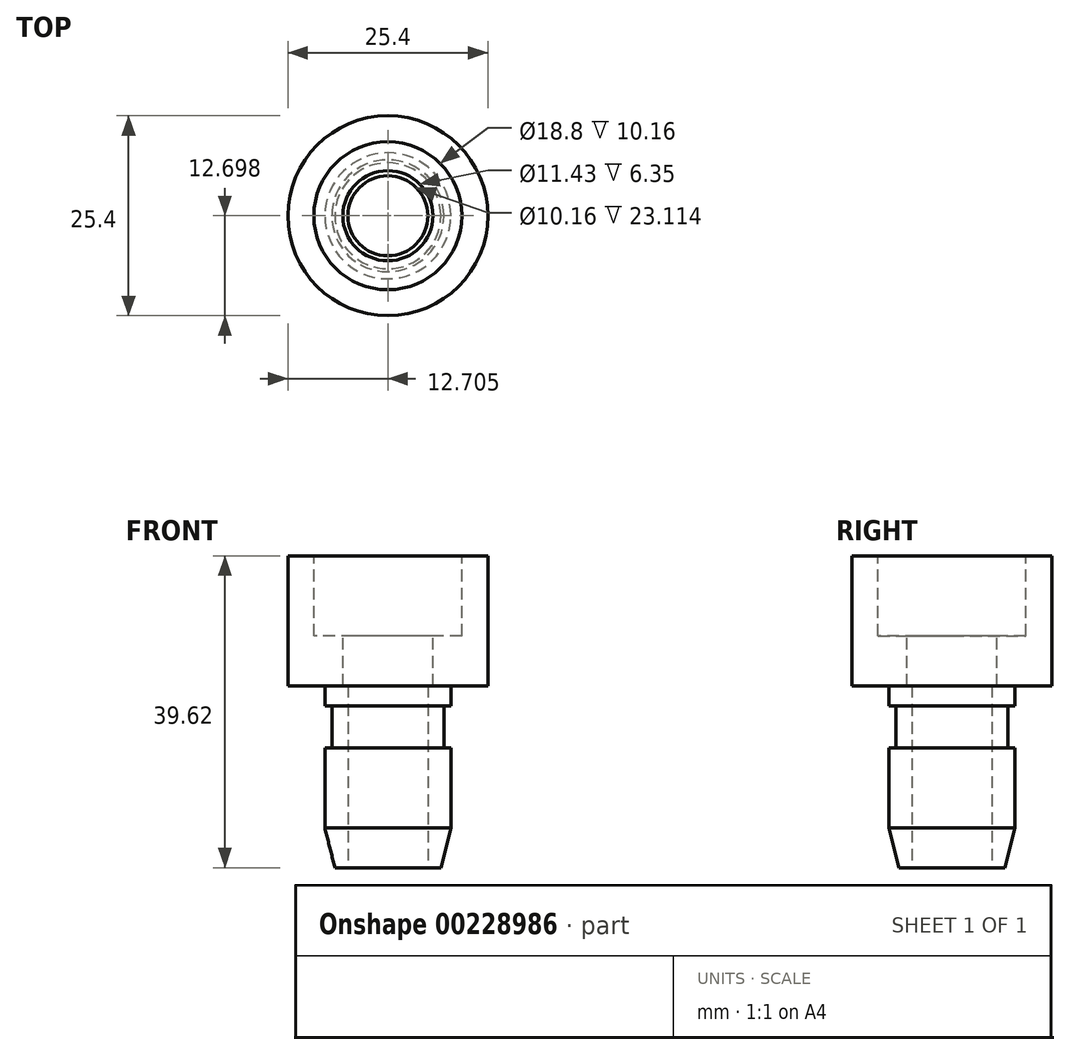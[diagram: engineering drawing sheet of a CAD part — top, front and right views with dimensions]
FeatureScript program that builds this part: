
annotation { "Feature Type Name" : "Feature", "Feature Type Description" : "" }
export const myFeature = defineFeature(function(context is Context, id is Id, definition is map)
    precondition{}
    {
        {
            var Q0;
            Q0=qCreatedBy(makeId("Top.planeOp"),FACE);
            var sketch = newSketch(context, id + "F0", { "sketchPlane" : qUnion([Q0])});
            skCircle(sketch, "E0", {"center": v(-47.56, -9.23) * mm, "radius": 12.7 * mm});
            skSolve(sketch);
        }
        {
            var Q0;
            Q0 = qSketchRegion(id + "F0", true);
            extrude(context, id + "F1", {"entities" : qUnion([Q0]), "oppositeDirection" : true, "depth" : 16.5 * mm});
        }
        {
            var Q0;
            Q0=makeQuery(id+"F1.opExtrude","CAP_FACE",FACE,{"disambiguationData":[OSD([sQuery(id+"F0.wireOp",EDGE,"E0")])],"isStart":true});
            var sketch = newSketch(context, id + "F2", { "sketchPlane" : qUnion([Q0])});
            skCircle(sketch, "E1", {"center": v(-47.56, -9.23) * mm, "radius": 9.4 * mm});
            skSolve(sketch);
        }
        {
            var Q0;
            Q0 = qSketchRegion(id + "F2", true);
            extrude(context, id + "F3", {"entities" : qUnion([Q0]), "operationType" : NewBodyOperationType.REMOVE, "oppositeDirection" : true, "depth" : 10.16 * mm});
        }
        {
            var Q0;
            Q0=makeQuery(id+"F3.boolean.opBoolean","COPY",FACE,{"derivedFrom":makeQuery(id+"F3.opExtrude","CAP_FACE",FACE,{"disambiguationData":[OSD([sQuery(id+"F2.wireOp",EDGE,"E1")])],"isStart":false})});
            var sketch = newSketch(context, id + "F4", { "sketchPlane" : qUnion([Q0])});
            skCircle(sketch, "E2", {"center": v(-47.56, -9.23) * mm, "radius": 5.72 * mm});
            skSolve(sketch);
        }
        {
            var Q0;
            Q0 = qSketchRegion(id + "F4", true);
            extrude(context, id + "F5", {"entities" : qUnion([Q0]), "operationType" : NewBodyOperationType.REMOVE, "oppositeDirection" : true, "depth" : 6.35 * mm});
        }
        {
            var Q0;
            Q0=makeQuery(id+"F1.opExtrude","CAP_FACE",FACE,{"disambiguationData":[OSD([sQuery(id+"F0.wireOp",EDGE,"E0")])],"isStart":false});
            var sketch = newSketch(context, id + "F6", { "sketchPlane" : qUnion([Q0])});
            skCircle(sketch, "E3", {"center": v(-47.56, 9.23) * mm, "radius": 8 * mm});
            skSolve(sketch);
        }
        {
            var Q0;
            Q0 = qSketchRegion(id + "F6", true);
            extrude(context, id + "F7", {"entities" : qUnion([Q0]), "operationType" : NewBodyOperationType.ADD, "depth" : 2.54 * mm});
        }
        {
            var Q0;
            Q0=makeQuery(id+"F7.opExtrude","CAP_FACE",FACE,{"disambiguationData":[OSD([sQuery(id+"F6.wireOp",EDGE,"E3")])],"isStart":false});
            var sketch = newSketch(context, id + "F8", { "sketchPlane" : qUnion([Q0])});
            skCircle(sketch, "E4", {"center": v(-47.56, 9.23) * mm, "radius": 7.11 * mm});
            skSolve(sketch);
        }
        {
            var Q0;
            Q0 = qSketchRegion(id + "F8", true);
            extrude(context, id + "F9", {"entities" : qUnion([Q0]), "operationType" : NewBodyOperationType.ADD, "depth" : 5.33 * mm});
        }
        {
            var Q0;
            Q0=makeQuery(id+"F9.opExtrude","CAP_FACE",FACE,{"disambiguationData":[OSD([sQuery(id+"F8.wireOp",EDGE,"E4")])],"isStart":false});
            var sketch = newSketch(context, id + "F10", { "sketchPlane" : qUnion([Q0])});
            skCircle(sketch, "E5", {"center": v(-47.56, 9.23) * mm, "radius": 8 * mm});
            skSolve(sketch);
        }
        {
            var Q0;
            Q0 = qSketchRegion(id + "F10", true);
            extrude(context, id + "F11", {"entities" : qUnion([Q0]), "operationType" : NewBodyOperationType.ADD, "depth" : 15.24 * mm});
        }
        {
            var Q0;
            Q0=makeQuery(id+"F11.opExtrude","CAP_EDGE",EDGE,{"disambiguationData":[OSD([sQuery(id+"F10.wireOp",EDGE,"E5")])],"isStart":false});
            chamfer(context, id + "F12", {"entities" : qUnion([Q0]), "chamferType" : ChamferType.TWO_OFFSETS, "width1" : 1.27 * mm, "oppositeDirection" : false, "width2" : 5.08 * mm, "tangentPropagation" : true});
        }
        {
            var Q0;
            Q0=makeQuery(id+"F11.opExtrude","CAP_FACE",FACE,{"disambiguationData":[OSD([sQuery(id+"F10.wireOp",EDGE,"E5")])],"isStart":false});
            var sketch = newSketch(context, id + "F13", { "sketchPlane" : qUnion([Q0])});
            skCircle(sketch, "E6", {"center": v(-47.56, 9.23) * mm, "radius": 5.08 * mm});
            skSolve(sketch);
        }
        {
            var Q0;
            Q0 = qSketchRegion(id + "F13", true);
            extrude(context, id + "F14", {"entities" : qUnion([Q0]), "operationType" : NewBodyOperationType.REMOVE, "oppositeDirection" : true, "depth" : 25.4 * mm});
        }
    });
